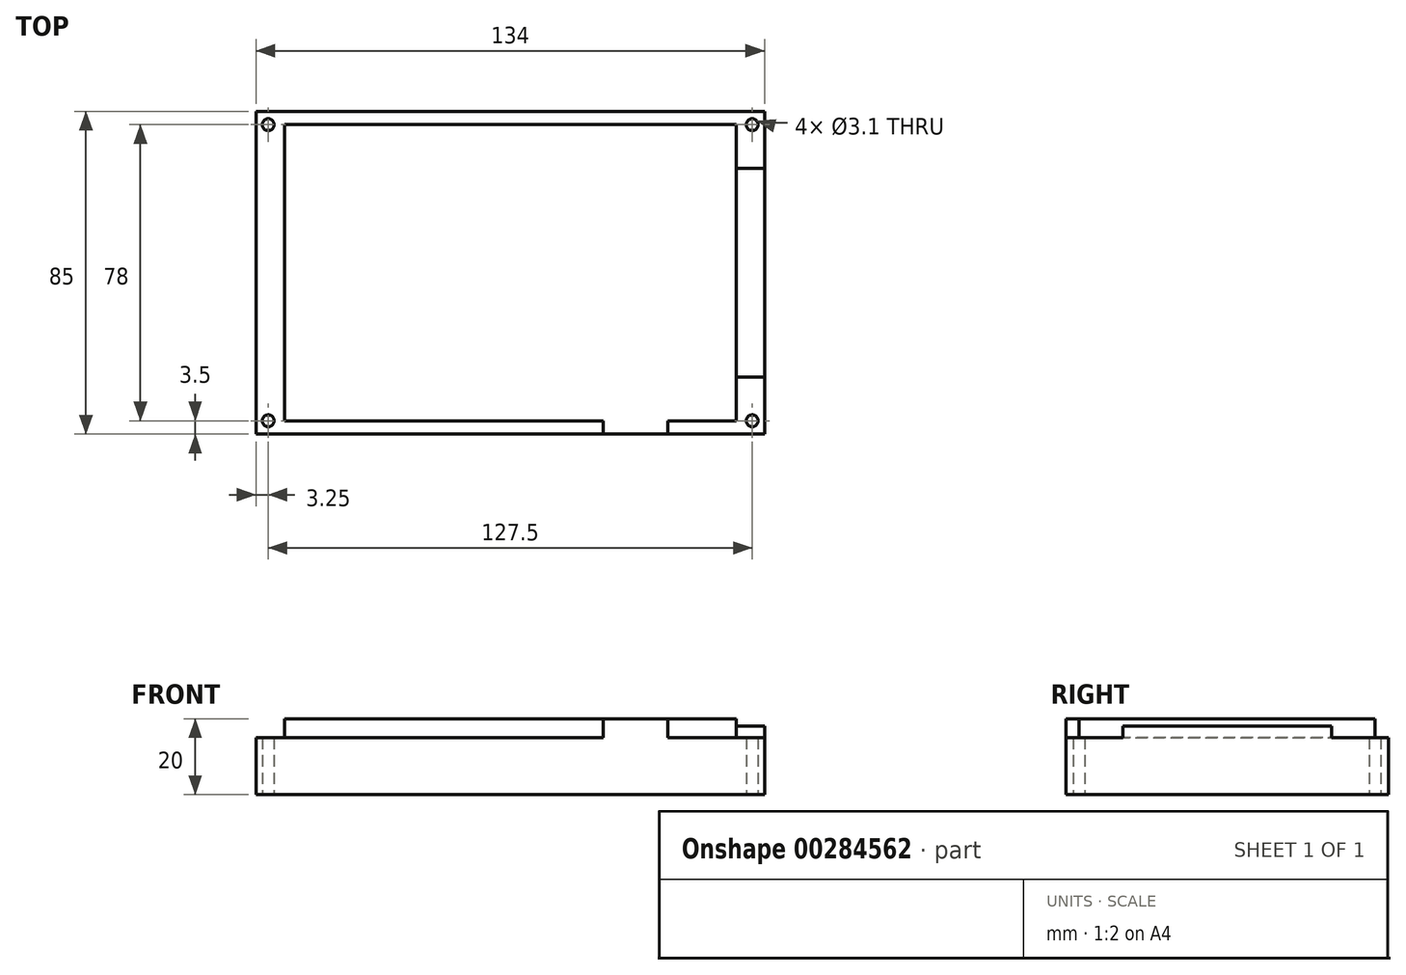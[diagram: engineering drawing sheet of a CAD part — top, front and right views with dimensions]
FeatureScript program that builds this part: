
annotation { "Feature Type Name" : "Feature", "Feature Type Description" : "" }
export const myFeature = defineFeature(function(context is Context, id is Id, definition is map)
    precondition{}
    {
        {
            var Q0;
            Q0=qCreatedBy(makeId("Top.planeOp"),FACE);
            var sketch = newSketch(context, id + "F0", { "sketchPlane" : qUnion([Q0])});
            skLineSegment(sketch, "E0.bottom", {"start": v(0, 0) * mm, "end": v(-134, 0) * mm});
            skLineSegment(sketch, "E0.top", {"start": v(0, 85) * mm, "end": v(-134, 85) * mm});
            skLineSegment(sketch, "E0.left", {"start": v(0, 0) * mm, "end": v(0, 85) * mm});
            skLineSegment(sketch, "E0.right", {"start": v(-134, 0) * mm, "end": v(-134, 85) * mm});
            skLineSegment(sketch, "E1", {"start": v(-134, 85) * mm, "end": v(-134, 81.5) * mm});
            skLineSegment(sketch, "E2", {"start": v(-134, 81.5) * mm, "end": v(-130.75, 81.5) * mm});
            skLineSegment(sketch, "E3", {"start": v(-134, 0) * mm, "end": v(-134, 3.5) * mm});
            skLineSegment(sketch, "E4", {"start": v(-134, 3.5) * mm, "end": v(-130.75, 3.5) * mm});
            skLineSegment(sketch, "E5", {"start": v(0, 85) * mm, "end": v(0, 81.5) * mm});
            skLineSegment(sketch, "E6", {"start": v(0, 81.5) * mm, "end": v(-3.25, 81.5) * mm});
            skLineSegment(sketch, "E7", {"start": v(0, 0) * mm, "end": v(0, 3.5) * mm});
            skLineSegment(sketch, "E8", {"start": v(0, 3.5) * mm, "end": v(-3.25, 3.5) * mm});
            skCircle(sketch, "E9", {"center": v(-130.75, 81.5) * mm, "radius": 1.55 * mm});
            skCircle(sketch, "E10", {"center": v(-130.75, 3.5) * mm, "radius": 1.55 * mm});
            skCircle(sketch, "E11", {"center": v(-3.25, 81.5) * mm, "radius": 1.55 * mm});
            skCircle(sketch, "E12", {"center": v(-3.25, 3.5) * mm, "radius": 1.55 * mm});
            skLineSegment(sketch, "E13", {"start": v(0, 81.5) * mm, "end": v(-7.5, 81.5) * mm});
            skSolve(sketch);
        }
        {
            var Q0;
            Q0 = qSketchRegion(id + "F0", true);
            extrude(context, id + "F1", {"entities" : qUnion([Q0]), "depth" : 15 * mm});
        }
        {
            var Q0;
            Q0=makeQuery(id+"F1.opExtrude","CAP_FACE",FACE,{"disambiguationData":[OSD([sQuery(id+"F0.wireOp",EDGE,"E0.bottom"),sQuery(id+"F0.wireOp",EDGE,"E0.top"),sQuery(id+"F0.wireOp",EDGE,"E0.left"),sQuery(id+"F0.wireOp",EDGE,"E0.right"),sQuery(id+"F0.wireOp",EDGE,"E1"),sQuery(id+"F0.wireOp",EDGE,"E3"),sQuery(id+"F0.wireOp",EDGE,"E5"),sQuery(id+"F0.wireOp",EDGE,"E7"),sQuery(id+"F0.wireOp",EDGE,"E9"),sQuery(id+"F0.wireOp",EDGE,"E10"),sQuery(id+"F0.wireOp",EDGE,"E11"),sQuery(id+"F0.wireOp",EDGE,"E12")])],"isStart":false});
            var sketch = newSketch(context, id + "F2", { "sketchPlane" : qUnion([Q0])});
            skLineSegment(sketch, "E14", {"start": v(0, 85) * mm, "end": v(-7.5, 85) * mm});
            skLineSegment(sketch, "E15", {"start": v(-7.5, 85) * mm, "end": v(-7.5, 81.5) * mm});
            skLineSegment(sketch, "E16", {"start": v(-134, 0) * mm, "end": v(-126.5, 0) * mm});
            skLineSegment(sketch, "E17", {"start": v(-126.5, 0) * mm, "end": v(-126.5, 3.5) * mm});
            skLineSegment(sketch, "E18.bottom", {"start": v(-7.5, 81.5) * mm, "end": v(-126.5, 81.5) * mm});
            skLineSegment(sketch, "E18.top", {"start": v(-7.5, 3.5) * mm, "end": v(-126.5, 3.5) * mm});
            skLineSegment(sketch, "E18.left", {"start": v(-7.5, 81.5) * mm, "end": v(-7.5, 3.5) * mm});
            skLineSegment(sketch, "E18.right", {"start": v(-126.5, 81.5) * mm, "end": v(-126.5, 3.5) * mm});
            skLineSegment(sketch, "E19", {"start": v(-7.5, 3.5) * mm, "end": v(-25.5, 3.5) * mm});
            skLineSegment(sketch, "E20", {"start": v(-25.5, 3.5) * mm, "end": v(-42.5, 3.5) * mm});
            skLineSegment(sketch, "E21", {"start": v(-42.5, 3.5) * mm, "end": v(-42.5, 0) * mm});
            skLineSegment(sketch, "E22.top", {"start": v(-25.5, 0) * mm, "end": v(-42.5, 0) * mm});
            skLineSegment(sketch, "E22.left", {"start": v(-25.5, 3.5) * mm, "end": v(-25.5, 0) * mm});
            skSolve(sketch);
        }
        {
            var Q0;
            Q0 = qSketchRegion(id + "F2", true);
            extrude(context, id + "F3", {"entities" : qUnion([Q0]), "operationType" : NewBodyOperationType.ADD, "depth" : 5 * mm});
        }
        {
            var Q0;
            Q0=makeQuery(id+"F1.opExtrude","CAP_FACE",FACE,{"disambiguationData":[OSD([sQuery(id+"F0.wireOp",EDGE,"E0.bottom"),sQuery(id+"F0.wireOp",EDGE,"E0.top"),sQuery(id+"F0.wireOp",EDGE,"E0.left"),sQuery(id+"F0.wireOp",EDGE,"E0.right"),sQuery(id+"F0.wireOp",EDGE,"E1"),sQuery(id+"F0.wireOp",EDGE,"E3"),sQuery(id+"F0.wireOp",EDGE,"E5"),sQuery(id+"F0.wireOp",EDGE,"E7"),sQuery(id+"F0.wireOp",EDGE,"E9"),sQuery(id+"F0.wireOp",EDGE,"E10"),sQuery(id+"F0.wireOp",EDGE,"E11"),sQuery(id+"F0.wireOp",EDGE,"E12")])],"isStart":false});
            var sketch = newSketch(context, id + "F4", { "sketchPlane" : qUnion([Q0])});
            skLineSegment(sketch, "E23", {"start": v(0, 85) * mm, "end": v(0, 70) * mm});
            skLineSegment(sketch, "E24", {"start": v(-7.5, 3.5) * mm, "end": v(-7.5, 15) * mm});
            skLineSegment(sketch, "E25.bottom", {"start": v(0, 70) * mm, "end": v(-7.5, 70) * mm});
            skLineSegment(sketch, "E25.top", {"start": v(0, 15) * mm, "end": v(-7.5, 15) * mm});
            skLineSegment(sketch, "E25.left", {"start": v(0, 70) * mm, "end": v(0, 15) * mm});
            skLineSegment(sketch, "E25.right", {"start": v(-7.5, 70) * mm, "end": v(-7.5, 15) * mm});
            skSolve(sketch);
        }
        {
            var Q0;
            Q0 = qSketchRegion(id + "F4", true);
            extrude(context, id + "F5", {"entities" : qUnion([Q0]), "operationType" : NewBodyOperationType.ADD, "depth" : 3 * mm});
        }
    });
